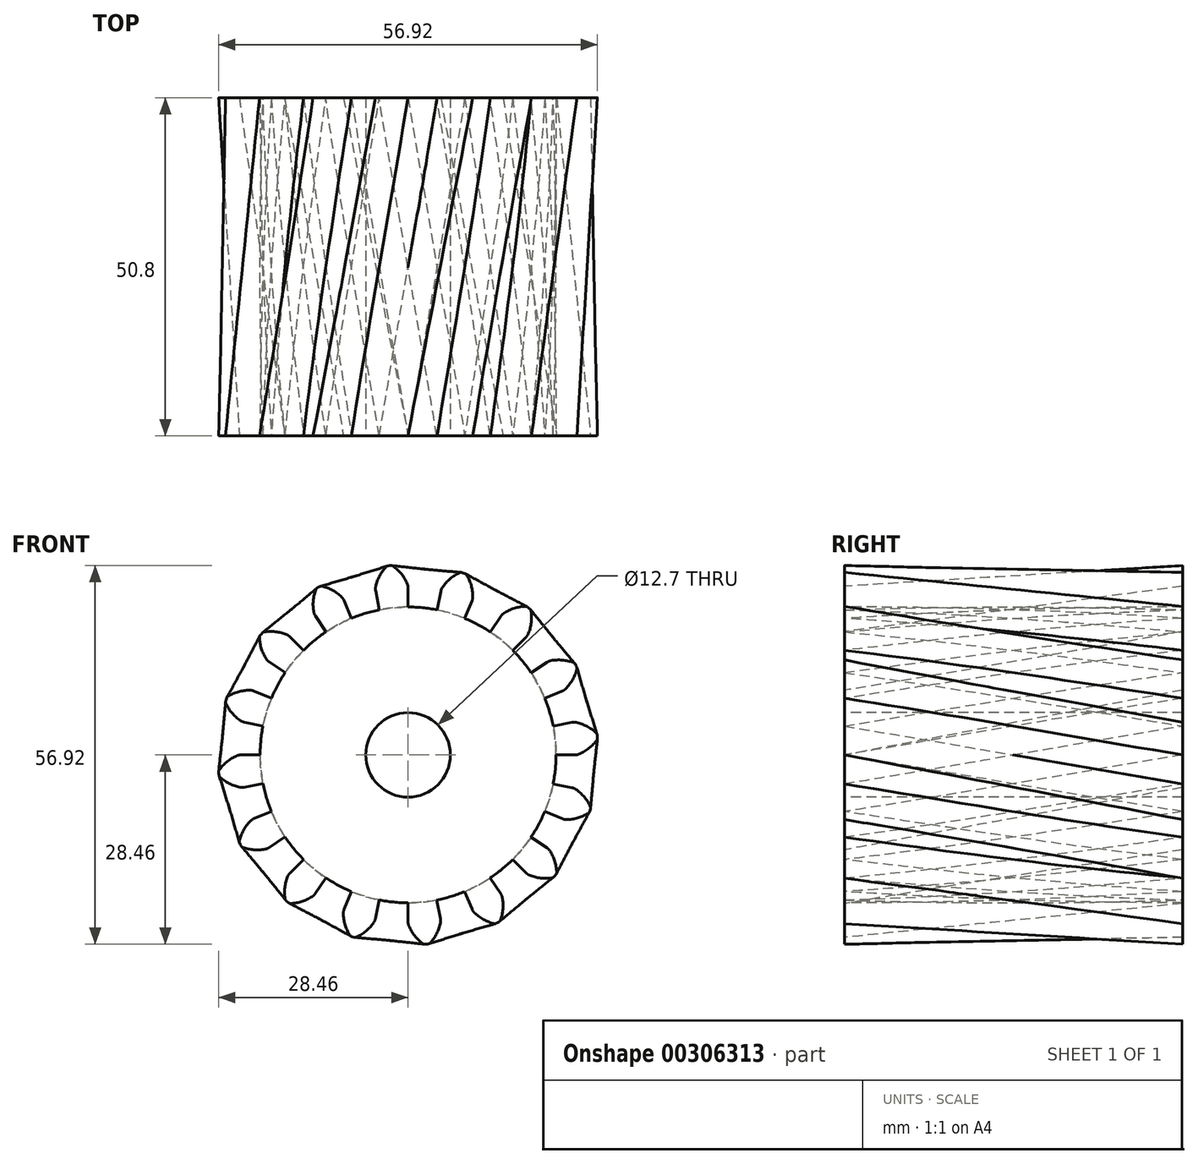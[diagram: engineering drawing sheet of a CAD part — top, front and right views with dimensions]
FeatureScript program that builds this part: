
annotation { "Feature Type Name" : "Feature", "Feature Type Description" : "" }
export const myFeature = defineFeature(function(context is Context, id is Id, definition is map)
    precondition{}
    {
        {
            var Q0;
            Q0=qCreatedBy(makeId("Front.planeOp"),FACE);
            var sketch = newSketch(context, id + "F0", { "sketchPlane" : qUnion([Q0])});
            skArc(sketch, "E0", {"start": v(-18.47, 12.36) * mm, "mid": v(-19.6, 10.49) * mm, "end": v(-20.53, 8.5) * mm});
            skArc(sketch, "E1.trimOffspring", {"start": v(-0.13, 25.72) * mm, "mid": v(-1, 27.18) * mm, "end": v(-2.23, 28.36) * mm});
            skLineSegment(sketch, "E2", {"start": v(0, 25.1) * mm, "end": v(0, 22.23) * mm});
            skLineSegment(sketch, "E3", {"start": v(-2.58, 28.46) * mm, "end": v(-2.79, 28.44) * mm});
            skArc(sketch, "E4.MirrorCS", {"start": v(-4.87, 25.26) * mm, "mid": v(-4.3, 26.86) * mm, "end": v(-3.32, 28.25) * mm});
            skLineSegment(sketch, "E5.MirrorCS", {"start": v(-4.88, 24.62) * mm, "end": v(-4.32, 21.8) * mm});
            skLineSegment(sketch, "E6.MirrorCS", {"start": v(-3, 28.42) * mm, "end": v(-2.79, 28.44) * mm});
            skPoint(sketch, "E7.visualSharp", {"position": v(-4.93, 24.92) * mm});
            skArc(sketch, "E7.filletArc", {"start": v(-4.87, 25.26) * mm, "mid": v(-4.9, 24.94) * mm, "end": v(-4.88, 24.62) * mm});
            skPoint(sketch, "E8.visualSharp", {"position": v(0, 25.4) * mm});
            skArc(sketch, "E8.filletArc", {"start": v(0, 25.1) * mm, "mid": v(-0.03, 25.42) * mm, "end": v(-0.13, 25.72) * mm});
            skPoint(sketch, "E9.visualSharp", {"position": v(-3.19, 28.4) * mm});
            skArc(sketch, "E9.filletArc", {"start": v(-3, 28.42) * mm, "mid": v(-3.17, 28.36) * mm, "end": v(-3.32, 28.25) * mm});
            skPoint(sketch, "E10.visualSharp", {"position": v(-2.4, 28.47) * mm});
            skArc(sketch, "E10.filletArc", {"start": v(-2.23, 28.36) * mm, "mid": v(-2.4, 28.44) * mm, "end": v(-2.58, 28.46) * mm});
            skArc(sketch, "E11.1.0", {"start": v(-14.17, 21.47) * mm, "mid": v(-14.25, 23.17) * mm, "end": v(-13.88, 24.83) * mm});
            skLineSegment(sketch, "E11.1.1", {"start": v(-13.93, 20.88) * mm, "end": v(-12.33, 18.5) * mm});
            skLineSegment(sketch, "E11.1.2", {"start": v(-9.6, 23.19) * mm, "end": v(-8.5, 20.53) * mm});
            skArc(sketch, "E11.1.3", {"start": v(-9.96, 23.72) * mm, "mid": v(-11.33, 24.73) * mm, "end": v(-12.91, 25.35) * mm});
            skArc(sketch, "E11.1.4", {"start": v(-9.6, 23.19) * mm, "mid": v(-9.76, 23.47) * mm, "end": v(-9.96, 23.72) * mm});
            skArc(sketch, "E11.1.5", {"start": v(-14.17, 21.47) * mm, "mid": v(-14.08, 21.16) * mm, "end": v(-13.93, 20.88) * mm});
            skArc(sketch, "E11.1.6", {"start": v(-13.64, 25.1) * mm, "mid": v(-13.79, 25) * mm, "end": v(-13.88, 24.83) * mm});
            skArc(sketch, "E11.1.7", {"start": v(-12.91, 25.35) * mm, "mid": v(-13.1, 25.36) * mm, "end": v(-13.27, 25.3) * mm});
            skLineSegment(sketch, "E11.1.8", {"start": v(-13.27, 25.3) * mm, "end": v(-13.46, 25.2) * mm});
            skLineSegment(sketch, "E11.1.9", {"start": v(-13.64, 25.1) * mm, "end": v(-13.46, 25.2) * mm});
            skArc(sketch, "E11.2.0", {"start": v(-21.3, 14.42) * mm, "mid": v(-22.03, 15.95) * mm, "end": v(-22.33, 17.63) * mm});
            skLineSegment(sketch, "E11.2.1", {"start": v(-20.86, 13.96) * mm, "end": v(-18.47, 12.36) * mm});
            skLineSegment(sketch, "E11.2.2", {"start": v(-17.75, 17.75) * mm, "end": v(-15.72, 15.72) * mm});
            skArc(sketch, "E11.2.3", {"start": v(-18.28, 18.1) * mm, "mid": v(-19.93, 18.52) * mm, "end": v(-21.63, 18.48) * mm});
            skArc(sketch, "E11.2.4", {"start": v(-17.75, 17.75) * mm, "mid": v(-18, 17.95) * mm, "end": v(-18.28, 18.1) * mm});
            skArc(sketch, "E11.2.5", {"start": v(-21.3, 14.42) * mm, "mid": v(-21.1, 14.17) * mm, "end": v(-20.86, 13.96) * mm});
            skArc(sketch, "E11.2.6", {"start": v(-22.21, 17.97) * mm, "mid": v(-22.3, 17.81) * mm, "end": v(-22.33, 17.63) * mm});
            skArc(sketch, "E11.2.7", {"start": v(-21.63, 18.48) * mm, "mid": v(-21.8, 18.42) * mm, "end": v(-21.94, 18.3) * mm});
            skLineSegment(sketch, "E11.2.8", {"start": v(-21.94, 18.3) * mm, "end": v(-22.08, 18.14) * mm});
            skLineSegment(sketch, "E11.2.9", {"start": v(-22.21, 17.97) * mm, "end": v(-22.08, 18.14) * mm});
            skLineSegment(sketch, "E12.4.3.0", {"start": v(-24.61, 4.92) * mm, "end": v(-21.8, 4.35) * mm});
            skArc(sketch, "E12.6.3.0", {"start": v(-25.2, 5.17) * mm, "mid": v(-26.46, 6.3) * mm, "end": v(-27.37, 7.74) * mm});
            skLineSegment(sketch, "E12.7.3.0", {"start": v(-23.19, 9.6) * mm, "end": v(-20.53, 8.5) * mm});
            skArc(sketch, "E12.10.3.0", {"start": v(-23.81, 9.73) * mm, "mid": v(-25.5, 9.48) * mm, "end": v(-27.06, 8.8) * mm});
            skArc(sketch, "E12.14.3.0", {"start": v(-23.19, 9.6) * mm, "mid": v(-23.5, 9.7) * mm, "end": v(-23.81, 9.73) * mm});
            skArc(sketch, "E12.18.3.0", {"start": v(-25.2, 5.17) * mm, "mid": v(-24.92, 5.01) * mm, "end": v(-24.61, 4.92) * mm});
            skArc(sketch, "E12.22.3.0", {"start": v(-27.4, 8.1) * mm, "mid": v(-27.42, 7.92) * mm, "end": v(-27.37, 7.74) * mm});
            skArc(sketch, "E12.26.3.0", {"start": v(-27.06, 8.8) * mm, "mid": v(-27.2, 8.67) * mm, "end": v(-27.28, 8.5) * mm});
            skLineSegment(sketch, "E12.30.3.0", {"start": v(-27.28, 8.5) * mm, "end": v(-27.34, 8.3) * mm});
            skLineSegment(sketch, "E12.33.3.0", {"start": v(-27.4, 8.1) * mm, "end": v(-27.34, 8.3) * mm});
            skLineSegment(sketch, "E12.4.4.0", {"start": v(-24.62, -4.88) * mm, "end": v(-21.8, -4.32) * mm});
            skArc(sketch, "E12.6.4.0", {"start": v(-25.26, -4.87) * mm, "mid": v(-26.86, -4.3) * mm, "end": v(-28.25, -3.32) * mm});
            skLineSegment(sketch, "E12.7.4.0", {"start": v(-25.1, 0) * mm, "end": v(-22.23, 0) * mm});
            skArc(sketch, "E12.10.4.0", {"start": v(-25.72, -0.13) * mm, "mid": v(-27.18, -1) * mm, "end": v(-28.36, -2.23) * mm});
            skArc(sketch, "E12.14.4.0", {"start": v(-25.1, 0) * mm, "mid": v(-25.42, -0.03) * mm, "end": v(-25.72, -0.13) * mm});
            skArc(sketch, "E12.18.4.0", {"start": v(-25.26, -4.87) * mm, "mid": v(-24.94, -4.9) * mm, "end": v(-24.62, -4.88) * mm});
            skArc(sketch, "E12.22.4.0", {"start": v(-28.42, -3) * mm, "mid": v(-28.36, -3.17) * mm, "end": v(-28.25, -3.32) * mm});
            skArc(sketch, "E12.26.4.0", {"start": v(-28.36, -2.23) * mm, "mid": v(-28.44, -2.4) * mm, "end": v(-28.46, -2.58) * mm});
            skLineSegment(sketch, "E12.30.4.0", {"start": v(-28.46, -2.58) * mm, "end": v(-28.44, -2.79) * mm});
            skLineSegment(sketch, "E12.33.4.0", {"start": v(-28.42, -3) * mm, "end": v(-28.44, -2.79) * mm});
            skLineSegment(sketch, "E12.4.5.0", {"start": v(-20.88, -13.93) * mm, "end": v(-18.5, -12.33) * mm});
            skArc(sketch, "E12.6.5.0", {"start": v(-21.47, -14.17) * mm, "mid": v(-23.17, -14.25) * mm, "end": v(-24.83, -13.88) * mm});
            skLineSegment(sketch, "E12.7.5.0", {"start": v(-23.19, -9.6) * mm, "end": v(-20.53, -8.5) * mm});
            skArc(sketch, "E12.10.5.0", {"start": v(-23.72, -9.96) * mm, "mid": v(-24.73, -11.33) * mm, "end": v(-25.35, -12.91) * mm});
            skArc(sketch, "E12.14.5.0", {"start": v(-23.19, -9.6) * mm, "mid": v(-23.47, -9.76) * mm, "end": v(-23.72, -9.96) * mm});
            skArc(sketch, "E12.18.5.0", {"start": v(-21.47, -14.17) * mm, "mid": v(-21.16, -14.08) * mm, "end": v(-20.88, -13.93) * mm});
            skArc(sketch, "E12.22.5.0", {"start": v(-25.1, -13.64) * mm, "mid": v(-25, -13.79) * mm, "end": v(-24.83, -13.88) * mm});
            skArc(sketch, "E12.26.5.0", {"start": v(-25.35, -12.91) * mm, "mid": v(-25.36, -13.1) * mm, "end": v(-25.3, -13.27) * mm});
            skLineSegment(sketch, "E12.30.5.0", {"start": v(-25.3, -13.27) * mm, "end": v(-25.2, -13.46) * mm});
            skLineSegment(sketch, "E12.33.5.0", {"start": v(-25.1, -13.64) * mm, "end": v(-25.2, -13.46) * mm});
            skLineSegment(sketch, "E12.4.6.0", {"start": v(-13.96, -20.86) * mm, "end": v(-12.36, -18.47) * mm});
            skArc(sketch, "E12.6.6.0", {"start": v(-14.42, -21.3) * mm, "mid": v(-15.95, -22.03) * mm, "end": v(-17.63, -22.33) * mm});
            skLineSegment(sketch, "E12.7.6.0", {"start": v(-17.75, -17.75) * mm, "end": v(-15.72, -15.72) * mm});
            skArc(sketch, "E12.10.6.0", {"start": v(-18.1, -18.28) * mm, "mid": v(-18.52, -19.93) * mm, "end": v(-18.48, -21.63) * mm});
            skArc(sketch, "E12.14.6.0", {"start": v(-17.75, -17.75) * mm, "mid": v(-17.95, -18) * mm, "end": v(-18.1, -18.28) * mm});
            skArc(sketch, "E12.18.6.0", {"start": v(-14.42, -21.3) * mm, "mid": v(-14.17, -21.1) * mm, "end": v(-13.96, -20.86) * mm});
            skArc(sketch, "E12.22.6.0", {"start": v(-17.97, -22.21) * mm, "mid": v(-17.81, -22.3) * mm, "end": v(-17.63, -22.33) * mm});
            skArc(sketch, "E12.26.6.0", {"start": v(-18.48, -21.63) * mm, "mid": v(-18.42, -21.8) * mm, "end": v(-18.3, -21.94) * mm});
            skLineSegment(sketch, "E12.30.6.0", {"start": v(-18.3, -21.94) * mm, "end": v(-18.14, -22.08) * mm});
            skLineSegment(sketch, "E12.33.6.0", {"start": v(-17.97, -22.21) * mm, "end": v(-18.14, -22.08) * mm});
            skLineSegment(sketch, "E12.4.7.0", {"start": v(-4.92, -24.61) * mm, "end": v(-4.35, -21.8) * mm});
            skArc(sketch, "E12.6.7.0", {"start": v(-5.17, -25.2) * mm, "mid": v(-6.3, -26.46) * mm, "end": v(-7.74, -27.37) * mm});
            skLineSegment(sketch, "E12.7.7.0", {"start": v(-9.6, -23.19) * mm, "end": v(-8.5, -20.53) * mm});
            skArc(sketch, "E12.10.7.0", {"start": v(-9.73, -23.81) * mm, "mid": v(-9.48, -25.5) * mm, "end": v(-8.8, -27.06) * mm});
            skArc(sketch, "E12.14.7.0", {"start": v(-9.6, -23.19) * mm, "mid": v(-9.7, -23.5) * mm, "end": v(-9.73, -23.81) * mm});
            skArc(sketch, "E12.18.7.0", {"start": v(-5.17, -25.2) * mm, "mid": v(-5.01, -24.92) * mm, "end": v(-4.92, -24.61) * mm});
            skArc(sketch, "E12.22.7.0", {"start": v(-8.1, -27.4) * mm, "mid": v(-7.92, -27.42) * mm, "end": v(-7.74, -27.37) * mm});
            skArc(sketch, "E12.26.7.0", {"start": v(-8.8, -27.06) * mm, "mid": v(-8.67, -27.2) * mm, "end": v(-8.5, -27.28) * mm});
            skLineSegment(sketch, "E12.30.7.0", {"start": v(-8.5, -27.28) * mm, "end": v(-8.3, -27.34) * mm});
            skLineSegment(sketch, "E12.33.7.0", {"start": v(-8.1, -27.4) * mm, "end": v(-8.3, -27.34) * mm});
            skLineSegment(sketch, "E12.4.8.0", {"start": v(4.88, -24.62) * mm, "end": v(4.32, -21.8) * mm});
            skArc(sketch, "E12.6.8.0", {"start": v(4.87, -25.26) * mm, "mid": v(4.3, -26.86) * mm, "end": v(3.32, -28.25) * mm});
            skLineSegment(sketch, "E12.7.8.0", {"start": v(0, -25.1) * mm, "end": v(0, -22.23) * mm});
            skArc(sketch, "E12.10.8.0", {"start": v(0.13, -25.72) * mm, "mid": v(1, -27.18) * mm, "end": v(2.23, -28.36) * mm});
            skArc(sketch, "E12.14.8.0", {"start": v(0, -25.1) * mm, "mid": v(0.03, -25.42) * mm, "end": v(0.13, -25.72) * mm});
            skArc(sketch, "E12.18.8.0", {"start": v(4.87, -25.26) * mm, "mid": v(4.9, -24.94) * mm, "end": v(4.88, -24.62) * mm});
            skArc(sketch, "E12.22.8.0", {"start": v(3, -28.42) * mm, "mid": v(3.17, -28.36) * mm, "end": v(3.32, -28.25) * mm});
            skArc(sketch, "E12.26.8.0", {"start": v(2.23, -28.36) * mm, "mid": v(2.4, -28.44) * mm, "end": v(2.58, -28.46) * mm});
            skLineSegment(sketch, "E12.30.8.0", {"start": v(2.58, -28.46) * mm, "end": v(2.79, -28.44) * mm});
            skLineSegment(sketch, "E12.33.8.0", {"start": v(3, -28.42) * mm, "end": v(2.79, -28.44) * mm});
            skLineSegment(sketch, "E12.4.9.0", {"start": v(13.93, -20.88) * mm, "end": v(12.33, -18.5) * mm});
            skArc(sketch, "E12.6.9.0", {"start": v(14.17, -21.47) * mm, "mid": v(14.25, -23.17) * mm, "end": v(13.88, -24.83) * mm});
            skLineSegment(sketch, "E12.7.9.0", {"start": v(9.6, -23.19) * mm, "end": v(8.5, -20.53) * mm});
            skArc(sketch, "E12.10.9.0", {"start": v(9.96, -23.72) * mm, "mid": v(11.33, -24.73) * mm, "end": v(12.91, -25.35) * mm});
            skArc(sketch, "E12.14.9.0", {"start": v(9.6, -23.19) * mm, "mid": v(9.76, -23.47) * mm, "end": v(9.96, -23.72) * mm});
            skArc(sketch, "E12.18.9.0", {"start": v(14.17, -21.47) * mm, "mid": v(14.08, -21.16) * mm, "end": v(13.93, -20.88) * mm});
            skArc(sketch, "E12.22.9.0", {"start": v(13.64, -25.1) * mm, "mid": v(13.79, -25) * mm, "end": v(13.88, -24.83) * mm});
            skArc(sketch, "E12.26.9.0", {"start": v(12.91, -25.35) * mm, "mid": v(13.1, -25.36) * mm, "end": v(13.27, -25.3) * mm});
            skLineSegment(sketch, "E12.30.9.0", {"start": v(13.27, -25.3) * mm, "end": v(13.46, -25.2) * mm});
            skLineSegment(sketch, "E12.33.9.0", {"start": v(13.64, -25.1) * mm, "end": v(13.46, -25.2) * mm});
            skLineSegment(sketch, "E12.4.10.0", {"start": v(20.86, -13.96) * mm, "end": v(18.47, -12.36) * mm});
            skArc(sketch, "E12.6.10.0", {"start": v(21.3, -14.42) * mm, "mid": v(22.03, -15.95) * mm, "end": v(22.33, -17.63) * mm});
            skLineSegment(sketch, "E12.7.10.0", {"start": v(17.75, -17.75) * mm, "end": v(15.72, -15.72) * mm});
            skArc(sketch, "E12.10.10.0", {"start": v(18.28, -18.1) * mm, "mid": v(19.93, -18.52) * mm, "end": v(21.63, -18.48) * mm});
            skArc(sketch, "E12.14.10.0", {"start": v(17.75, -17.75) * mm, "mid": v(18, -17.95) * mm, "end": v(18.28, -18.1) * mm});
            skArc(sketch, "E12.18.10.0", {"start": v(21.3, -14.42) * mm, "mid": v(21.1, -14.17) * mm, "end": v(20.86, -13.96) * mm});
            skArc(sketch, "E12.22.10.0", {"start": v(22.21, -17.97) * mm, "mid": v(22.3, -17.81) * mm, "end": v(22.33, -17.63) * mm});
            skArc(sketch, "E12.26.10.0", {"start": v(21.63, -18.48) * mm, "mid": v(21.8, -18.42) * mm, "end": v(21.94, -18.3) * mm});
            skLineSegment(sketch, "E12.30.10.0", {"start": v(21.94, -18.3) * mm, "end": v(22.08, -18.14) * mm});
            skLineSegment(sketch, "E12.33.10.0", {"start": v(22.21, -17.97) * mm, "end": v(22.08, -18.14) * mm});
            skLineSegment(sketch, "E12.4.11.0", {"start": v(24.61, -4.92) * mm, "end": v(21.8, -4.35) * mm});
            skArc(sketch, "E12.6.11.0", {"start": v(25.2, -5.17) * mm, "mid": v(26.46, -6.3) * mm, "end": v(27.37, -7.74) * mm});
            skLineSegment(sketch, "E12.7.11.0", {"start": v(23.19, -9.6) * mm, "end": v(20.53, -8.5) * mm});
            skArc(sketch, "E12.10.11.0", {"start": v(23.81, -9.73) * mm, "mid": v(25.5, -9.48) * mm, "end": v(27.06, -8.8) * mm});
            skArc(sketch, "E12.14.11.0", {"start": v(23.19, -9.6) * mm, "mid": v(23.5, -9.7) * mm, "end": v(23.81, -9.73) * mm});
            skArc(sketch, "E12.18.11.0", {"start": v(25.2, -5.17) * mm, "mid": v(24.92, -5.01) * mm, "end": v(24.61, -4.92) * mm});
            skArc(sketch, "E12.22.11.0", {"start": v(27.4, -8.1) * mm, "mid": v(27.42, -7.92) * mm, "end": v(27.37, -7.74) * mm});
            skArc(sketch, "E12.26.11.0", {"start": v(27.06, -8.8) * mm, "mid": v(27.2, -8.67) * mm, "end": v(27.28, -8.5) * mm});
            skLineSegment(sketch, "E12.30.11.0", {"start": v(27.28, -8.5) * mm, "end": v(27.34, -8.3) * mm});
            skLineSegment(sketch, "E12.33.11.0", {"start": v(27.4, -8.1) * mm, "end": v(27.34, -8.3) * mm});
            skLineSegment(sketch, "E12.4.12.0", {"start": v(24.62, 4.88) * mm, "end": v(21.8, 4.32) * mm});
            skArc(sketch, "E12.6.12.0", {"start": v(25.26, 4.87) * mm, "mid": v(26.86, 4.3) * mm, "end": v(28.25, 3.32) * mm});
            skLineSegment(sketch, "E12.7.12.0", {"start": v(25.1, 0) * mm, "end": v(22.23, 0) * mm});
            skArc(sketch, "E12.10.12.0", {"start": v(25.72, 0.13) * mm, "mid": v(27.18, 1) * mm, "end": v(28.36, 2.23) * mm});
            skArc(sketch, "E12.14.12.0", {"start": v(25.1, 0) * mm, "mid": v(25.42, 0.03) * mm, "end": v(25.72, 0.13) * mm});
            skArc(sketch, "E12.18.12.0", {"start": v(25.26, 4.87) * mm, "mid": v(24.94, 4.9) * mm, "end": v(24.62, 4.88) * mm});
            skArc(sketch, "E12.22.12.0", {"start": v(28.42, 3) * mm, "mid": v(28.36, 3.17) * mm, "end": v(28.25, 3.32) * mm});
            skArc(sketch, "E12.26.12.0", {"start": v(28.36, 2.23) * mm, "mid": v(28.44, 2.4) * mm, "end": v(28.46, 2.58) * mm});
            skLineSegment(sketch, "E12.30.12.0", {"start": v(28.46, 2.58) * mm, "end": v(28.44, 2.79) * mm});
            skLineSegment(sketch, "E12.33.12.0", {"start": v(28.42, 3) * mm, "end": v(28.44, 2.79) * mm});
            skLineSegment(sketch, "E12.4.13.0", {"start": v(20.88, 13.93) * mm, "end": v(18.5, 12.33) * mm});
            skArc(sketch, "E12.6.13.0", {"start": v(21.47, 14.17) * mm, "mid": v(23.17, 14.25) * mm, "end": v(24.83, 13.88) * mm});
            skLineSegment(sketch, "E12.7.13.0", {"start": v(23.19, 9.6) * mm, "end": v(20.53, 8.5) * mm});
            skArc(sketch, "E12.10.13.0", {"start": v(23.72, 9.96) * mm, "mid": v(24.73, 11.33) * mm, "end": v(25.35, 12.91) * mm});
            skArc(sketch, "E12.14.13.0", {"start": v(23.19, 9.6) * mm, "mid": v(23.47, 9.76) * mm, "end": v(23.72, 9.96) * mm});
            skArc(sketch, "E12.18.13.0", {"start": v(21.47, 14.17) * mm, "mid": v(21.16, 14.08) * mm, "end": v(20.88, 13.93) * mm});
            skArc(sketch, "E12.22.13.0", {"start": v(25.1, 13.64) * mm, "mid": v(25, 13.79) * mm, "end": v(24.83, 13.88) * mm});
            skArc(sketch, "E12.26.13.0", {"start": v(25.35, 12.91) * mm, "mid": v(25.36, 13.1) * mm, "end": v(25.3, 13.27) * mm});
            skLineSegment(sketch, "E12.30.13.0", {"start": v(25.3, 13.27) * mm, "end": v(25.2, 13.46) * mm});
            skLineSegment(sketch, "E12.33.13.0", {"start": v(25.1, 13.64) * mm, "end": v(25.2, 13.46) * mm});
            skLineSegment(sketch, "E12.4.14.0", {"start": v(13.96, 20.86) * mm, "end": v(12.36, 18.47) * mm});
            skArc(sketch, "E12.6.14.0", {"start": v(14.42, 21.3) * mm, "mid": v(15.95, 22.03) * mm, "end": v(17.63, 22.33) * mm});
            skLineSegment(sketch, "E12.7.14.0", {"start": v(17.75, 17.75) * mm, "end": v(15.72, 15.72) * mm});
            skArc(sketch, "E12.10.14.0", {"start": v(18.1, 18.28) * mm, "mid": v(18.52, 19.93) * mm, "end": v(18.48, 21.63) * mm});
            skArc(sketch, "E12.14.14.0", {"start": v(17.75, 17.75) * mm, "mid": v(17.95, 18) * mm, "end": v(18.1, 18.28) * mm});
            skArc(sketch, "E12.18.14.0", {"start": v(14.42, 21.3) * mm, "mid": v(14.17, 21.1) * mm, "end": v(13.96, 20.86) * mm});
            skArc(sketch, "E12.22.14.0", {"start": v(17.97, 22.21) * mm, "mid": v(17.81, 22.3) * mm, "end": v(17.63, 22.33) * mm});
            skArc(sketch, "E12.26.14.0", {"start": v(18.48, 21.63) * mm, "mid": v(18.42, 21.8) * mm, "end": v(18.3, 21.94) * mm});
            skLineSegment(sketch, "E12.30.14.0", {"start": v(18.3, 21.94) * mm, "end": v(18.14, 22.08) * mm});
            skLineSegment(sketch, "E12.33.14.0", {"start": v(17.97, 22.21) * mm, "end": v(18.14, 22.08) * mm});
            skLineSegment(sketch, "E12.4.15.0", {"start": v(4.92, 24.61) * mm, "end": v(4.35, 21.8) * mm});
            skArc(sketch, "E12.6.15.0", {"start": v(5.17, 25.2) * mm, "mid": v(6.3, 26.46) * mm, "end": v(7.74, 27.37) * mm});
            skLineSegment(sketch, "E12.7.15.0", {"start": v(9.6, 23.19) * mm, "end": v(8.5, 20.53) * mm});
            skArc(sketch, "E12.10.15.0", {"start": v(9.73, 23.81) * mm, "mid": v(9.48, 25.5) * mm, "end": v(8.8, 27.06) * mm});
            skArc(sketch, "E12.14.15.0", {"start": v(9.6, 23.19) * mm, "mid": v(9.7, 23.5) * mm, "end": v(9.73, 23.81) * mm});
            skArc(sketch, "E12.18.15.0", {"start": v(5.17, 25.2) * mm, "mid": v(5.01, 24.92) * mm, "end": v(4.92, 24.61) * mm});
            skArc(sketch, "E12.22.15.0", {"start": v(8.1, 27.4) * mm, "mid": v(7.92, 27.42) * mm, "end": v(7.74, 27.37) * mm});
            skArc(sketch, "E12.26.15.0", {"start": v(8.8, 27.06) * mm, "mid": v(8.67, 27.2) * mm, "end": v(8.5, 27.28) * mm});
            skLineSegment(sketch, "E12.30.15.0", {"start": v(8.5, 27.28) * mm, "end": v(8.3, 27.34) * mm});
            skLineSegment(sketch, "E12.33.15.0", {"start": v(8.1, 27.4) * mm, "end": v(8.3, 27.34) * mm});
            skArc(sketch, "E13.trimOffspring", {"start": v(-12.33, 18.5) * mm, "mid": v(-14.1, 17.19) * mm, "end": v(-15.72, 15.72) * mm});
            skArc(sketch, "E14.trimOffspring", {"start": v(-4.32, 21.8) * mm, "mid": v(-6.44, 21.27) * mm, "end": v(-8.5, 20.53) * mm});
            skArc(sketch, "E15.trimOffspring", {"start": v(4.35, 21.8) * mm, "mid": v(2.19, 22.12) * mm, "end": v(0, 22.23) * mm});
            skArc(sketch, "E16.trimOffspring", {"start": v(12.36, 18.47) * mm, "mid": v(10.49, 19.6) * mm, "end": v(8.5, 20.53) * mm});
            skArc(sketch, "E17.trimOffspring", {"start": v(18.5, 12.33) * mm, "mid": v(17.19, 14.1) * mm, "end": v(15.72, 15.72) * mm});
            skArc(sketch, "E18.trimOffspring", {"start": v(21.8, 4.32) * mm, "mid": v(21.27, 6.44) * mm, "end": v(20.53, 8.5) * mm});
            skArc(sketch, "E19.trimOffspring", {"start": v(21.8, -4.35) * mm, "mid": v(22.12, -2.19) * mm, "end": v(22.23, 0) * mm});
            skArc(sketch, "E20.trimOffspring", {"start": v(12.33, -18.5) * mm, "mid": v(14.1, -17.19) * mm, "end": v(15.72, -15.72) * mm});
            skArc(sketch, "E21.trimOffspring", {"start": v(18.47, -12.36) * mm, "mid": v(19.6, -10.49) * mm, "end": v(20.53, -8.5) * mm});
            skArc(sketch, "E22.trimOffspring", {"start": v(4.32, -21.8) * mm, "mid": v(6.44, -21.27) * mm, "end": v(8.5, -20.53) * mm});
            skArc(sketch, "E23.trimOffspring", {"start": v(-4.35, -21.8) * mm, "mid": v(-2.19, -22.12) * mm, "end": v(0, -22.22) * mm});
            skArc(sketch, "E24.trimOffspring", {"start": v(-12.36, -18.47) * mm, "mid": v(-10.49, -19.6) * mm, "end": v(-8.5, -20.53) * mm});
            skArc(sketch, "E25.trimOffspring", {"start": v(-18.5, -12.33) * mm, "mid": v(-17.19, -14.1) * mm, "end": v(-15.72, -15.72) * mm});
            skArc(sketch, "E26.trimOffspring", {"start": v(-21.8, -4.32) * mm, "mid": v(-21.27, -6.44) * mm, "end": v(-20.53, -8.5) * mm});
            skArc(sketch, "E27.trimOffspring", {"start": v(-21.8, 4.35) * mm, "mid": v(-22.12, 2.19) * mm, "end": v(-22.22, 0) * mm});
            skCircle(sketch, "E28", {"center": v(0, 0) * mm, "radius": 22.23 * mm});
            skSolve(sketch);
        }
        {
            var Q0;
            Q0=qCreatedBy(makeId("Front.planeOp"),FACE);
            cPlane(context, id + "F1", {"entities" : qUnion([Q0]), "cplaneType" : CPlaneType.OFFSET, "offset" : 50.8 * mm, "width" : 152.4 * mm, "height" : 152.4 * mm});
        }
        {
            var Q0;
            Q0=qCreatedBy(id+"F1.planeOp",FACE);
            var sketch = newSketch(context, id + "F2", { "sketchPlane" : qUnion([Q0])});
            skArc(sketch, "E29.0.0", {"start": v(22.23, 0) * mm, "mid": v(22.12, 2.17) * mm, "end": v(21.8, 4.32) * mm});
            skArc(sketch, "E29.0.1", {"start": v(21.8, 4.32) * mm, "mid": v(21.27, 6.44) * mm, "end": v(20.53, 8.5) * mm});
            skArc(sketch, "E29.0.2", {"start": v(20.53, 8.5) * mm, "mid": v(19.6, 10.47) * mm, "end": v(18.5, 12.33) * mm});
            skArc(sketch, "E29.0.3", {"start": v(18.5, 12.33) * mm, "mid": v(17.19, 14.1) * mm, "end": v(15.72, 15.72) * mm});
            skArc(sketch, "E29.0.4", {"start": v(15.72, 15.72) * mm, "mid": v(14.1, 17.17) * mm, "end": v(12.36, 18.47) * mm});
            skArc(sketch, "E29.0.5", {"start": v(12.36, 18.47) * mm, "mid": v(10.49, 19.6) * mm, "end": v(8.5, 20.53) * mm});
            skArc(sketch, "E29.0.6", {"start": v(8.5, 20.53) * mm, "mid": v(6.46, 21.27) * mm, "end": v(4.35, 21.8) * mm});
            skArc(sketch, "E29.0.7", {"start": v(4.35, 21.8) * mm, "mid": v(2.19, 22.12) * mm, "end": v(0, 22.23) * mm});
            skArc(sketch, "E29.0.8", {"start": v(0, 22.23) * mm, "mid": v(-2.17, 22.12) * mm, "end": v(-4.32, 21.8) * mm});
            skArc(sketch, "E29.0.9", {"start": v(-4.32, 21.8) * mm, "mid": v(-6.44, 21.27) * mm, "end": v(-8.5, 20.53) * mm});
            skArc(sketch, "E29.0.10", {"start": v(-8.5, 20.53) * mm, "mid": v(-10.47, 19.6) * mm, "end": v(-12.33, 18.5) * mm});
            skArc(sketch, "E29.0.11", {"start": v(-12.33, 18.5) * mm, "mid": v(-14.1, 17.19) * mm, "end": v(-15.72, 15.72) * mm});
            skArc(sketch, "E29.0.12", {"start": v(-15.72, 15.72) * mm, "mid": v(-17.17, 14.1) * mm, "end": v(-18.47, 12.36) * mm});
            skArc(sketch, "E29.0.13", {"start": v(-18.47, 12.36) * mm, "mid": v(-19.6, 10.49) * mm, "end": v(-20.53, 8.5) * mm});
            skArc(sketch, "E29.0.14", {"start": v(-20.53, 8.5) * mm, "mid": v(-21.27, 6.46) * mm, "end": v(-21.8, 4.35) * mm});
            skArc(sketch, "E29.0.15", {"start": v(-21.8, 4.35) * mm, "mid": v(-22.12, 2.19) * mm, "end": v(-22.22, 0) * mm});
            skArc(sketch, "E29.0.16", {"start": v(-22.23, 0) * mm, "mid": v(-22.12, -2.17) * mm, "end": v(-21.8, -4.32) * mm});
            skArc(sketch, "E29.0.17", {"start": v(-21.8, -4.32) * mm, "mid": v(-21.27, -6.44) * mm, "end": v(-20.53, -8.5) * mm});
            skArc(sketch, "E29.0.18", {"start": v(-20.53, -8.5) * mm, "mid": v(-19.6, -10.47) * mm, "end": v(-18.5, -12.33) * mm});
            skArc(sketch, "E29.0.19", {"start": v(-18.5, -12.33) * mm, "mid": v(-17.19, -14.1) * mm, "end": v(-15.72, -15.72) * mm});
            skArc(sketch, "E29.0.20", {"start": v(-15.72, -15.72) * mm, "mid": v(-14.1, -17.17) * mm, "end": v(-12.36, -18.47) * mm});
            skArc(sketch, "E29.0.21", {"start": v(-12.36, -18.47) * mm, "mid": v(-10.49, -19.6) * mm, "end": v(-8.5, -20.53) * mm});
            skArc(sketch, "E29.0.22", {"start": v(-8.5, -20.53) * mm, "mid": v(-6.46, -21.27) * mm, "end": v(-4.35, -21.8) * mm});
            skArc(sketch, "E29.0.23", {"start": v(-4.35, -21.8) * mm, "mid": v(-2.19, -22.12) * mm, "end": v(0, -22.22) * mm});
            skArc(sketch, "E29.0.24", {"start": v(0, -22.23) * mm, "mid": v(2.17, -22.12) * mm, "end": v(4.32, -21.8) * mm});
            skArc(sketch, "E29.0.25", {"start": v(4.32, -21.8) * mm, "mid": v(6.44, -21.27) * mm, "end": v(8.5, -20.53) * mm});
            skArc(sketch, "E29.0.26", {"start": v(8.5, -20.53) * mm, "mid": v(10.47, -19.6) * mm, "end": v(12.33, -18.5) * mm});
            skArc(sketch, "E29.0.27", {"start": v(12.33, -18.5) * mm, "mid": v(14.1, -17.19) * mm, "end": v(15.72, -15.72) * mm});
            skArc(sketch, "E29.0.28", {"start": v(15.72, -15.72) * mm, "mid": v(17.17, -14.1) * mm, "end": v(18.47, -12.36) * mm});
            skArc(sketch, "E29.0.29", {"start": v(18.47, -12.36) * mm, "mid": v(19.6, -10.49) * mm, "end": v(20.53, -8.5) * mm});
            skArc(sketch, "E29.0.30", {"start": v(20.53, -8.5) * mm, "mid": v(21.27, -6.46) * mm, "end": v(21.8, -4.35) * mm});
            skArc(sketch, "E29.0.31", {"start": v(21.8, -4.35) * mm, "mid": v(22.12, -2.19) * mm, "end": v(22.23, 0) * mm});
            skArc(sketch, "E30.0.0", {"start": v(-3.32, 28.25) * mm, "mid": v(-4.3, 26.86) * mm, "end": v(-4.87, 25.26) * mm});
            skArc(sketch, "E30.0.1", {"start": v(-4.87, 25.26) * mm, "mid": v(-4.9, 24.94) * mm, "end": v(-4.88, 24.62) * mm});
            skLineSegment(sketch, "E30.0.2", {"start": v(-4.88, 24.62) * mm, "end": v(-4.32, 21.8) * mm});
            skArc(sketch, "E30.0.3", {"start": v(-4.32, 21.8) * mm, "mid": v(-2.17, 22.12) * mm, "end": v(0, 22.23) * mm});
            skLineSegment(sketch, "E30.0.4", {"start": v(0, 22.23) * mm, "end": v(0, 25.1) * mm});
            skArc(sketch, "E30.0.5", {"start": v(0, 25.1) * mm, "mid": v(-0.03, 25.42) * mm, "end": v(-0.13, 25.72) * mm});
            skArc(sketch, "E30.0.6", {"start": v(-0.13, 25.72) * mm, "mid": v(-1, 27.18) * mm, "end": v(-2.23, 28.36) * mm});
            skArc(sketch, "E30.0.7", {"start": v(-2.23, 28.36) * mm, "mid": v(-2.4, 28.44) * mm, "end": v(-2.58, 28.46) * mm});
            skLineSegment(sketch, "E30.0.8", {"start": v(-2.58, 28.46) * mm, "end": v(-2.79, 28.44) * mm});
            skLineSegment(sketch, "E30.0.9", {"start": v(-2.79, 28.44) * mm, "end": v(-3, 28.42) * mm});
            skArc(sketch, "E30.0.10", {"start": v(-3, 28.42) * mm, "mid": v(-3.17, 28.36) * mm, "end": v(-3.32, 28.25) * mm});
            skSolve(sketch);
        }
        {
            var Q0;
            Q0=makeQuery(id+"F2.imprint","IMPRINT",FACE,{"disambiguationData":[TD([[makeQuery(id+"F2.imprint","IMPRINT",EDGE,{"derivedFrom":sQuery(id+"F2.wireOp",EDGE,"E30.0.0")}),1.0]])]});
            var Q1;
            {var subQ0=sQuery(id+"F0.wireOp",EDGE,"E12.4.15.0");Q1=makeQuery(id+"F0.imprint","IMPRINT",FACE,{"disambiguationData":[TD([[makeQuery(id+"F0.imprint","IMPRINT",EDGE,{"derivedFrom":subQ0}),1.0]])]});}
            loft(context, id + "F3", {"sheetProfilesArray" : [{ "sheetProfileEntities" : qUnion([Q0]) }, { "sheetProfileEntities" : qUnion([Q1]) }]});
        }
        {
            var Q0;
            Q0=qCreatedBy(id+"F1.planeOp",FACE);
            var sketch = newSketch(context, id + "F4", { "sketchPlane" : qUnion([Q0])});
            skCircle(sketch, "E31", {"center": v(0, 0) * mm, "radius": 22.22 * mm});
            skSolve(sketch);
        }
        {
            var Q0;
            Q0=makeQuery(id+"F4.imprint","IMPRINT",FACE,{"disambiguationData":[TD([[makeQuery(id+"F4.imprint","IMPRINT",EDGE,{"derivedFrom":sQuery(id+"F4.wireOp",EDGE,"E31")}),1.0]])]});
            var Q1;
            {var subQ0=sQuery(id+"F0.wireOp",EDGE,"E12.4.15.0");Q1=makeQuery(id+"F3.opLoft","CAP_FACE",FACE,{"disambiguationData":[OSD([makeQuery(id+"F0.imprint","IMPRINT",FACE,{"disambiguationData":[TD([[makeQuery(id+"F0.imprint","IMPRINT",EDGE,{"derivedFrom":subQ0}),1.0]])]})])],"isStart":true});}
            extrude(context, id + "F5", {"entities" : qUnion([Q0]), "operationType" : NewBodyOperationType.ADD, "endBound" : BoundingType.UP_TO_SURFACE, "oppositeDirection" : true, "endBoundEntityFace" : qUnion([Q1]), "depth" : 25.4 * mm});
        }
        {
            var Q0;
            {var subQ0=sQuery(id+"F0.wireOp",EDGE,"E12.4.15.0");Q0=makeQuery(id+"F3.opLoft","SWEPT_BODY",BODY,{"disambiguationData":[OSD([makeQuery(id+"F0.imprint","IMPRINT",FACE,{"disambiguationData":[TD([[makeQuery(id+"F0.imprint","IMPRINT",EDGE,{"derivedFrom":subQ0}),1.0]])]}),makeQuery(id+"F2.imprint","IMPRINT",FACE,{"disambiguationData":[TD([[makeQuery(id+"F2.imprint","IMPRINT",EDGE,{"derivedFrom":sQuery(id+"F2.wireOp",EDGE,"E30.0.0")}),1.0]])]})])]});}
            var Q1;
            Q1=makeQuery(id+"F5.opExtrude","SWEPT_FACE",FACE,{"disambiguationData":[OSD([sQuery(id+"F4.wireOp",EDGE,"E31")])]});
            circularPattern(context, id + "F6", {"entities" : qUnion([Q0]), "axis" : qUnion([Q1]), "angle" : 360 * degree, "instanceCount" : 16, "equalSpace" : true});
        }
        {
            var Q0;
            {var subQ0=sQuery(id+"F0.wireOp",EDGE,"E12.4.15.0");Q0=makeQuery(id+"F6.opPattern","COPY",BODY,{"derivedFrom":makeQuery(id+"F3.opLoft","SWEPT_BODY",BODY,{"disambiguationData":[OSD([makeQuery(id+"F0.imprint","IMPRINT",FACE,{"disambiguationData":[TD([[makeQuery(id+"F0.imprint","IMPRINT",EDGE,{"derivedFrom":subQ0}),1.0]])]}),makeQuery(id+"F2.imprint","IMPRINT",FACE,{"disambiguationData":[TD([[makeQuery(id+"F2.imprint","IMPRINT",EDGE,{"derivedFrom":sQuery(id+"F2.wireOp",EDGE,"E30.0.0")}),1.0]])]})])]}),"instanceName":"13"});}
            var Q1;
            {var subQ0=sQuery(id+"F0.wireOp",EDGE,"E12.4.15.0");Q1=makeQuery(id+"F6.opPattern","COPY",BODY,{"derivedFrom":makeQuery(id+"F3.opLoft","SWEPT_BODY",BODY,{"disambiguationData":[OSD([makeQuery(id+"F0.imprint","IMPRINT",FACE,{"disambiguationData":[TD([[makeQuery(id+"F0.imprint","IMPRINT",EDGE,{"derivedFrom":subQ0}),1.0]])]}),makeQuery(id+"F2.imprint","IMPRINT",FACE,{"disambiguationData":[TD([[makeQuery(id+"F2.imprint","IMPRINT",EDGE,{"derivedFrom":sQuery(id+"F2.wireOp",EDGE,"E30.0.0")}),1.0]])]})])]}),"instanceName":"2"});}
            var Q2;
            {var subQ0=sQuery(id+"F0.wireOp",EDGE,"E12.4.15.0");Q2=makeQuery(id+"F6.opPattern","COPY",BODY,{"derivedFrom":makeQuery(id+"F3.opLoft","SWEPT_BODY",BODY,{"disambiguationData":[OSD([makeQuery(id+"F0.imprint","IMPRINT",FACE,{"disambiguationData":[TD([[makeQuery(id+"F0.imprint","IMPRINT",EDGE,{"derivedFrom":subQ0}),1.0]])]}),makeQuery(id+"F2.imprint","IMPRINT",FACE,{"disambiguationData":[TD([[makeQuery(id+"F2.imprint","IMPRINT",EDGE,{"derivedFrom":sQuery(id+"F2.wireOp",EDGE,"E30.0.0")}),1.0]])]})])]}),"instanceName":"8"});}
            var Q3;
            {var subQ0=sQuery(id+"F0.wireOp",EDGE,"E12.4.15.0");Q3=makeQuery(id+"F6.opPattern","COPY",BODY,{"derivedFrom":makeQuery(id+"F3.opLoft","SWEPT_BODY",BODY,{"disambiguationData":[OSD([makeQuery(id+"F0.imprint","IMPRINT",FACE,{"disambiguationData":[TD([[makeQuery(id+"F0.imprint","IMPRINT",EDGE,{"derivedFrom":subQ0}),1.0]])]}),makeQuery(id+"F2.imprint","IMPRINT",FACE,{"disambiguationData":[TD([[makeQuery(id+"F2.imprint","IMPRINT",EDGE,{"derivedFrom":sQuery(id+"F2.wireOp",EDGE,"E30.0.0")}),1.0]])]})])]}),"instanceName":"1"});}
            var Q4;
            {var subQ0=sQuery(id+"F0.wireOp",EDGE,"E12.4.15.0");Q4=makeQuery(id+"F3.opLoft","SWEPT_BODY",BODY,{"disambiguationData":[OSD([makeQuery(id+"F0.imprint","IMPRINT",FACE,{"disambiguationData":[TD([[makeQuery(id+"F0.imprint","IMPRINT",EDGE,{"derivedFrom":subQ0}),1.0]])]}),makeQuery(id+"F2.imprint","IMPRINT",FACE,{"disambiguationData":[TD([[makeQuery(id+"F2.imprint","IMPRINT",EDGE,{"derivedFrom":sQuery(id+"F2.wireOp",EDGE,"E30.0.0")}),1.0]])]})])]});}
            var Q5;
            {var subQ0=sQuery(id+"F0.wireOp",EDGE,"E12.4.15.0");Q5=makeQuery(id+"F6.opPattern","COPY",BODY,{"derivedFrom":makeQuery(id+"F3.opLoft","SWEPT_BODY",BODY,{"disambiguationData":[OSD([makeQuery(id+"F0.imprint","IMPRINT",FACE,{"disambiguationData":[TD([[makeQuery(id+"F0.imprint","IMPRINT",EDGE,{"derivedFrom":subQ0}),1.0]])]}),makeQuery(id+"F2.imprint","IMPRINT",FACE,{"disambiguationData":[TD([[makeQuery(id+"F2.imprint","IMPRINT",EDGE,{"derivedFrom":sQuery(id+"F2.wireOp",EDGE,"E30.0.0")}),1.0]])]})])]}),"instanceName":"15"});}
            var Q6;
            {var subQ0=sQuery(id+"F0.wireOp",EDGE,"E12.4.15.0");Q6=makeQuery(id+"F6.opPattern","COPY",BODY,{"derivedFrom":makeQuery(id+"F3.opLoft","SWEPT_BODY",BODY,{"disambiguationData":[OSD([makeQuery(id+"F0.imprint","IMPRINT",FACE,{"disambiguationData":[TD([[makeQuery(id+"F0.imprint","IMPRINT",EDGE,{"derivedFrom":subQ0}),1.0]])]}),makeQuery(id+"F2.imprint","IMPRINT",FACE,{"disambiguationData":[TD([[makeQuery(id+"F2.imprint","IMPRINT",EDGE,{"derivedFrom":sQuery(id+"F2.wireOp",EDGE,"E30.0.0")}),1.0]])]})])]}),"instanceName":"4"});}
            var Q7;
            {var subQ0=sQuery(id+"F0.wireOp",EDGE,"E12.4.15.0");Q7=makeQuery(id+"F6.opPattern","COPY",BODY,{"derivedFrom":makeQuery(id+"F3.opLoft","SWEPT_BODY",BODY,{"disambiguationData":[OSD([makeQuery(id+"F0.imprint","IMPRINT",FACE,{"disambiguationData":[TD([[makeQuery(id+"F0.imprint","IMPRINT",EDGE,{"derivedFrom":subQ0}),1.0]])]}),makeQuery(id+"F2.imprint","IMPRINT",FACE,{"disambiguationData":[TD([[makeQuery(id+"F2.imprint","IMPRINT",EDGE,{"derivedFrom":sQuery(id+"F2.wireOp",EDGE,"E30.0.0")}),1.0]])]})])]}),"instanceName":"14"});}
            var Q8;
            {var subQ0=sQuery(id+"F0.wireOp",EDGE,"E12.4.15.0");Q8=makeQuery(id+"F6.opPattern","COPY",BODY,{"derivedFrom":makeQuery(id+"F3.opLoft","SWEPT_BODY",BODY,{"disambiguationData":[OSD([makeQuery(id+"F0.imprint","IMPRINT",FACE,{"disambiguationData":[TD([[makeQuery(id+"F0.imprint","IMPRINT",EDGE,{"derivedFrom":subQ0}),1.0]])]}),makeQuery(id+"F2.imprint","IMPRINT",FACE,{"disambiguationData":[TD([[makeQuery(id+"F2.imprint","IMPRINT",EDGE,{"derivedFrom":sQuery(id+"F2.wireOp",EDGE,"E30.0.0")}),1.0]])]})])]}),"instanceName":"11"});}
            var Q9;
            {var subQ0=sQuery(id+"F0.wireOp",EDGE,"E12.4.15.0");Q9=makeQuery(id+"F6.opPattern","COPY",BODY,{"derivedFrom":makeQuery(id+"F3.opLoft","SWEPT_BODY",BODY,{"disambiguationData":[OSD([makeQuery(id+"F0.imprint","IMPRINT",FACE,{"disambiguationData":[TD([[makeQuery(id+"F0.imprint","IMPRINT",EDGE,{"derivedFrom":subQ0}),1.0]])]}),makeQuery(id+"F2.imprint","IMPRINT",FACE,{"disambiguationData":[TD([[makeQuery(id+"F2.imprint","IMPRINT",EDGE,{"derivedFrom":sQuery(id+"F2.wireOp",EDGE,"E30.0.0")}),1.0]])]})])]}),"instanceName":"10"});}
            var Q10;
            {var subQ0=sQuery(id+"F0.wireOp",EDGE,"E12.4.15.0");Q10=makeQuery(id+"F6.opPattern","COPY",BODY,{"derivedFrom":makeQuery(id+"F3.opLoft","SWEPT_BODY",BODY,{"disambiguationData":[OSD([makeQuery(id+"F0.imprint","IMPRINT",FACE,{"disambiguationData":[TD([[makeQuery(id+"F0.imprint","IMPRINT",EDGE,{"derivedFrom":subQ0}),1.0]])]}),makeQuery(id+"F2.imprint","IMPRINT",FACE,{"disambiguationData":[TD([[makeQuery(id+"F2.imprint","IMPRINT",EDGE,{"derivedFrom":sQuery(id+"F2.wireOp",EDGE,"E30.0.0")}),1.0]])]})])]}),"instanceName":"12"});}
            var Q11;
            {var subQ0=sQuery(id+"F0.wireOp",EDGE,"E12.4.15.0");Q11=makeQuery(id+"F6.opPattern","COPY",BODY,{"derivedFrom":makeQuery(id+"F3.opLoft","SWEPT_BODY",BODY,{"disambiguationData":[OSD([makeQuery(id+"F0.imprint","IMPRINT",FACE,{"disambiguationData":[TD([[makeQuery(id+"F0.imprint","IMPRINT",EDGE,{"derivedFrom":subQ0}),1.0]])]}),makeQuery(id+"F2.imprint","IMPRINT",FACE,{"disambiguationData":[TD([[makeQuery(id+"F2.imprint","IMPRINT",EDGE,{"derivedFrom":sQuery(id+"F2.wireOp",EDGE,"E30.0.0")}),1.0]])]})])]}),"instanceName":"9"});}
            var Q12;
            {var subQ0=sQuery(id+"F0.wireOp",EDGE,"E12.4.15.0");Q12=makeQuery(id+"F6.opPattern","COPY",BODY,{"derivedFrom":makeQuery(id+"F3.opLoft","SWEPT_BODY",BODY,{"disambiguationData":[OSD([makeQuery(id+"F0.imprint","IMPRINT",FACE,{"disambiguationData":[TD([[makeQuery(id+"F0.imprint","IMPRINT",EDGE,{"derivedFrom":subQ0}),1.0]])]}),makeQuery(id+"F2.imprint","IMPRINT",FACE,{"disambiguationData":[TD([[makeQuery(id+"F2.imprint","IMPRINT",EDGE,{"derivedFrom":sQuery(id+"F2.wireOp",EDGE,"E30.0.0")}),1.0]])]})])]}),"instanceName":"7"});}
            var Q13;
            {var subQ0=sQuery(id+"F0.wireOp",EDGE,"E12.4.15.0");Q13=makeQuery(id+"F6.opPattern","COPY",BODY,{"derivedFrom":makeQuery(id+"F3.opLoft","SWEPT_BODY",BODY,{"disambiguationData":[OSD([makeQuery(id+"F0.imprint","IMPRINT",FACE,{"disambiguationData":[TD([[makeQuery(id+"F0.imprint","IMPRINT",EDGE,{"derivedFrom":subQ0}),1.0]])]}),makeQuery(id+"F2.imprint","IMPRINT",FACE,{"disambiguationData":[TD([[makeQuery(id+"F2.imprint","IMPRINT",EDGE,{"derivedFrom":sQuery(id+"F2.wireOp",EDGE,"E30.0.0")}),1.0]])]})])]}),"instanceName":"3"});}
            var Q14;
            {var subQ0=sQuery(id+"F0.wireOp",EDGE,"E12.4.15.0");Q14=makeQuery(id+"F6.opPattern","COPY",BODY,{"derivedFrom":makeQuery(id+"F3.opLoft","SWEPT_BODY",BODY,{"disambiguationData":[OSD([makeQuery(id+"F0.imprint","IMPRINT",FACE,{"disambiguationData":[TD([[makeQuery(id+"F0.imprint","IMPRINT",EDGE,{"derivedFrom":subQ0}),1.0]])]}),makeQuery(id+"F2.imprint","IMPRINT",FACE,{"disambiguationData":[TD([[makeQuery(id+"F2.imprint","IMPRINT",EDGE,{"derivedFrom":sQuery(id+"F2.wireOp",EDGE,"E30.0.0")}),1.0]])]})])]}),"instanceName":"5"});}
            var Q15;
            {var subQ0=sQuery(id+"F0.wireOp",EDGE,"E12.4.15.0");Q15=makeQuery(id+"F6.opPattern","COPY",BODY,{"derivedFrom":makeQuery(id+"F3.opLoft","SWEPT_BODY",BODY,{"disambiguationData":[OSD([makeQuery(id+"F0.imprint","IMPRINT",FACE,{"disambiguationData":[TD([[makeQuery(id+"F0.imprint","IMPRINT",EDGE,{"derivedFrom":subQ0}),1.0]])]}),makeQuery(id+"F2.imprint","IMPRINT",FACE,{"disambiguationData":[TD([[makeQuery(id+"F2.imprint","IMPRINT",EDGE,{"derivedFrom":sQuery(id+"F2.wireOp",EDGE,"E30.0.0")}),1.0]])]})])]}),"instanceName":"6"});}
            booleanBodies(context, id + "F7", {"operationType" : BooleanOperationType.UNION, "tools" : qUnion([Q0, Q1, Q2, Q3, Q4, Q5, Q6, Q7, Q8, Q9, Q10, Q11, Q12, Q13, Q14, Q15])});
        }
        {
            var Q0;
            {var subQ0=makeQuery(id+"F5.boolean.opBoolean","MERGE",FACE,{"derivedFrom":[makeQuery(id+"F3.opLoft","CAP_FACE",FACE,{"disambiguationData":[OSD([makeQuery(id+"F2.imprint","IMPRINT",FACE,{"disambiguationData":[TD([[makeQuery(id+"F2.imprint","IMPRINT",EDGE,{"derivedFrom":sQuery(id+"F2.wireOp",EDGE,"E30.0.0")}),1.0]])]})])],"isStart":true}),makeQuery(id+"F5.opExtrude","CAP_FACE",FACE,{"disambiguationData":[OSD([sQuery(id+"F4.wireOp",EDGE,"E31")])],"isStart":true})]});Q0=makeQuery(id+"F7.opBoolean","MERGE",FACE,{"derivedFrom":[subQ0,makeQuery(id+"F6.opPattern","COPY",FACE,{"derivedFrom":subQ0,"instanceName":"1"}),makeQuery(id+"F6.opPattern","COPY",FACE,{"derivedFrom":subQ0,"instanceName":"2"}),makeQuery(id+"F6.opPattern","COPY",FACE,{"derivedFrom":subQ0,"instanceName":"3"}),makeQuery(id+"F6.opPattern","COPY",FACE,{"derivedFrom":subQ0,"instanceName":"4"}),makeQuery(id+"F6.opPattern","COPY",FACE,{"derivedFrom":subQ0,"instanceName":"5"}),makeQuery(id+"F6.opPattern","COPY",FACE,{"derivedFrom":subQ0,"instanceName":"6"}),makeQuery(id+"F6.opPattern","COPY",FACE,{"derivedFrom":subQ0,"instanceName":"7"}),makeQuery(id+"F6.opPattern","COPY",FACE,{"derivedFrom":subQ0,"instanceName":"8"}),makeQuery(id+"F6.opPattern","COPY",FACE,{"derivedFrom":subQ0,"instanceName":"9"}),makeQuery(id+"F6.opPattern","COPY",FACE,{"derivedFrom":subQ0,"instanceName":"10"}),makeQuery(id+"F6.opPattern","COPY",FACE,{"derivedFrom":subQ0,"instanceName":"11"}),makeQuery(id+"F6.opPattern","COPY",FACE,{"derivedFrom":subQ0,"instanceName":"12"}),makeQuery(id+"F6.opPattern","COPY",FACE,{"derivedFrom":subQ0,"instanceName":"13"}),makeQuery(id+"F6.opPattern","COPY",FACE,{"derivedFrom":subQ0,"instanceName":"14"}),makeQuery(id+"F6.opPattern","COPY",FACE,{"derivedFrom":subQ0,"instanceName":"15"})]});}
            var sketch = newSketch(context, id + "F8", { "sketchPlane" : qUnion([Q0])});
            skCircle(sketch, "E32", {"center": v(0, 0) * mm, "radius": 6.35 * mm});
            skSolve(sketch);
        }
        {
            var Q0;
            Q0 = qSketchRegion(id + "F8", true);
            extrude(context, id + "F9", {"entities" : qUnion([Q0]), "operationType" : NewBodyOperationType.REMOVE, "endBound" : BoundingType.THROUGH_ALL, "oppositeDirection" : true, "depth" : 25.4 * mm});
        }
    });
